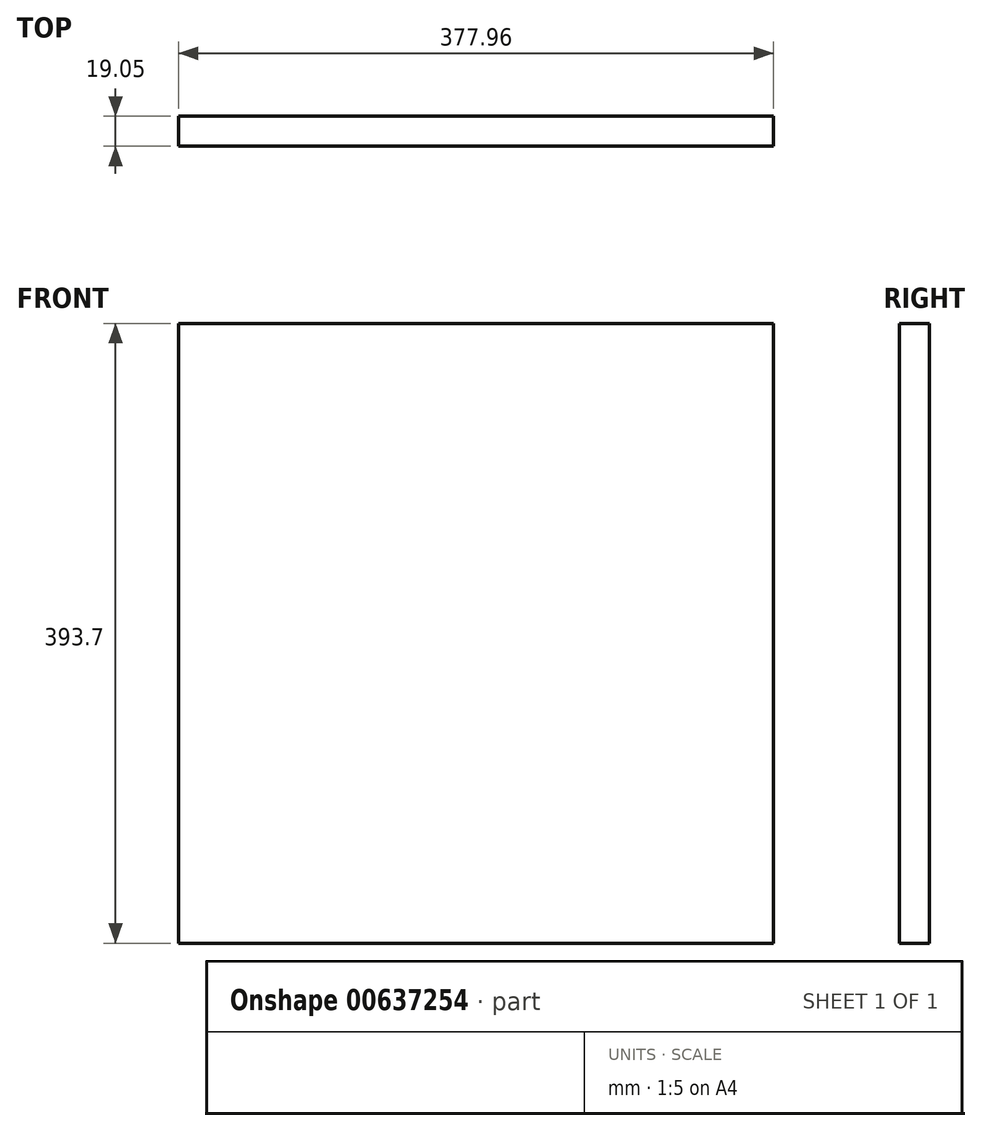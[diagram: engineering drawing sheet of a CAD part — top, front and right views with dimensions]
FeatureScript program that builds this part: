
annotation { "Feature Type Name" : "Feature", "Feature Type Description" : "" }
export const myFeature = defineFeature(function(context is Context, id is Id, definition is map)
    precondition{}
    {
        {
            var Q0;
            Q0=qCreatedBy(makeId("Front.planeOp"),FACE);
            var sketch = newSketch(context, id + "F0", { "sketchPlane" : qUnion([Q0])});
            skLineSegment(sketch, "E0.bottom", {"start": v(-188.98, 196.85) * mm, "end": v(188.98, 196.85) * mm});
            skLineSegment(sketch, "E0.top", {"start": v(-188.98, -196.85) * mm, "end": v(188.98, -196.85) * mm});
            skLineSegment(sketch, "E0.left", {"start": v(-188.98, 196.85) * mm, "end": v(-188.98, -196.85) * mm});
            skLineSegment(sketch, "E0.right", {"start": v(188.98, 196.85) * mm, "end": v(188.98, -196.85) * mm});
            skPoint(sketch, "E0.middle", {"position": v(0, 0) * mm});
            skSolve(sketch);
        }
        {
            var Q0;
            Q0=makeQuery(id+"F0.imprint","IMPRINT",FACE,{"disambiguationData":[TD([[makeQuery(id+"F0.imprint","IMPRINT",EDGE,{"derivedFrom":sQuery(id+"F0.wireOp",EDGE,"E0.bottom")}),-1.0]])]});
            extrude(context, id + "F1", {"entities" : qUnion([Q0]), "depth" : 19.05 * mm, "offsetDistance" : 25.4 * mm});
        }
    });
